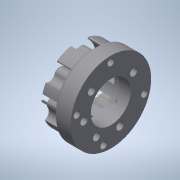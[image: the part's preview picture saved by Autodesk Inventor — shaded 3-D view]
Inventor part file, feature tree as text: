
AUTODESK INVENTOR PART (.ipt)
format: ipt  version: 2020 (Build 240168000, 168)  size: 658,432 bytes
history: native  units: in
note: dims shown in document units (in); Inventor stores cm internally (conversion verified against a paired STEP export)
features: sketch x21, extrude x7, other x4, plane x2
ambient origin geometry x8: Origin, YZ Plane, XZ Plane, XY Plane, X Axis, Y Axis, Z Axis, Center Point
bodies: Solid1 (feature_tree)
feature tree (34):
  other  "Mecanum Adaptor 1.3.ipt"
  extrude  "Extrusion1"  Depth=0.1378in
  extrude  "Extrusion2"  Depth=0.1406in
  extrude  "Extrusion3"  Depth=0.157in TaperAngle=0.0deg
  extrude  "Extrusion4"  Depth=0.1406in
  extrude  "Extrusion5"  Depth=0.1406in
  extrude  "Extrusion6"  Depth=0.512in TaperAngle=0.0deg
  extrude  "Extrusion7"  [1 undecoded]
  other  "Solid1::Mecanum Adaptor 1.3.ipt"
  other  "TaggingFeature1"
  sketch  "Sketch1"  dims[d0=0.3937in]
  sketch  "Sketch3"  dims[d4=0.4724in d5=0.0in d6=0.0787in d7=1.757in d8=1.6061in d9=0.0in d10=90.0deg d11=0.0in d12=90.0deg d13=0.1181in d14=0.0in d15=0.1575in d16=2.7559in d21=0.0in d23=0.0in d25=0.0in d26=0.1575in d27=0.0in d28=0.374in d29=2.7559in d33=0.0787in d34=0.0in d35=0.1378in d36=0.0in d38=0.0in d55=2.7559in d60=0.0in d61=0.2756in d62=0.7874in d64=0.446in d65=0.7874in d67=0.446in d70=0.0984in d71=0.0in d72=0.2638in d73=0.1575in d75=0.2638in d76=0.1575in d78=0.2638in d79=0.1575in d81=0.2638in d82=0.1575in d84=0.2638in d85=0.1575in d87=0.2638in d88=0.1575in d90=0.2638in d91=0.1575in d93=0.1575in d2=360.0deg d18=360.0deg d31=360.0deg d57=360.0deg d1=0.875in]
  sketch  "Sketch4"  dims[d3=1.0in d17=0.0in d19=0.1406in]
  sketch  "Sketch5"  dims[d20=1.0in d22=0.0in d24=0.157in d30=0.0in]
  sketch  "Sketch6"  dims[d32=0.158in d37=0.0in d40=0.1406in]
  sketch  "Sketch7"  dims[d41=0.1406in d42=0.1406in]
  sketch  "Sketch8"  dims[d43=1.7205in d44=0.0in d45=0.512in d46=0.0in]
  sketch  "Sketch9"  dims[d51=0.2in d52=0.0in]
  sketch  "Sketch10"
  sketch  "Sketch11"
  sketch  "Sketch12"
  sketch  "Sketch14"
  sketch  "Sketch16"
  sketch  "Sketch17"
  plane  "Work Plane1"
  plane  "Work Plane2"
  other  "Work Axis1"
  sketch  "Sketch18"
  sketch  "Sketch19"
  sketch  "Sketch20"
  sketch  "Sketch21"
  sketch  "Sketch22"
  sketch  "Sketch23"
  sketch  "Sketch24"
note: 1 required parameter value undecoded (feature->parameter linkage not recoverable at this tier; creation-order binding heuristic only, values carry confidence <= 0.55)
